# Revit family: QF_TRUE_TBR72-RISZ1-L-B-GGG-1
name_source: partatom
category: Specialty Equipment
revit_build: Autodesk Revit 2016 (Build: 20150714_1515(x64)
units: mm (PartAtom-declared; Revit-internal decimal feet)

## family parameters
Always vertical = Yes
Cut with Voids When Loaded = No
Part Type = Normal
Room Calculation Point = No
Round Connector Dimension = Use Diameter
Shared = No
Work Plane-Based = No

## types (1)
- QF_TRUE_TBR72-RISZ1-L-B-GGG-1
    Apparent Power = 207 VA
    Conn Conduit = Yes
    Conn Plug = NEMA 5-15P
    Cycle = 60 Hz
    Depth = 26 3/8"
    Description = REACH-IN SINGLE ZONE REFRIGERATOR WITH LEFT SIDE REFRIGERATION SYSTEM. BLACK EXTERIOR AND GLASS SWING DOORS
    Elec Conn Connection Height = 0"
    Elec Conn RI Height = 0"
    FL Amps = 2 A
    Foodservice Equipment Identifier = Yes
    HP = 1/5
    Identify Quantity as Lot = Yes
    Indirect Waste Connection Height = 0"
    Indirect Waste Flow = 0 GPM
    Indirect Waste Size = 1"
    Length = 72"
    Manufacturer = TRUE
    Max Overcurrent Protection = 0 A
    Min Ckt Ampacity = 0 A
    Model = TBR72-RISZ1-L-B-GGG-1
    Number of Poles = 1
    Phase = 1
    Volts = 115 V
    Waste Water Discharge Temperature = -460 °F
    Watts = 207 W
    Weight in Pounds = 0

## geometry (parser evidence)
native form markers: Sweep x19
no freeform markers — native parametric forms only
